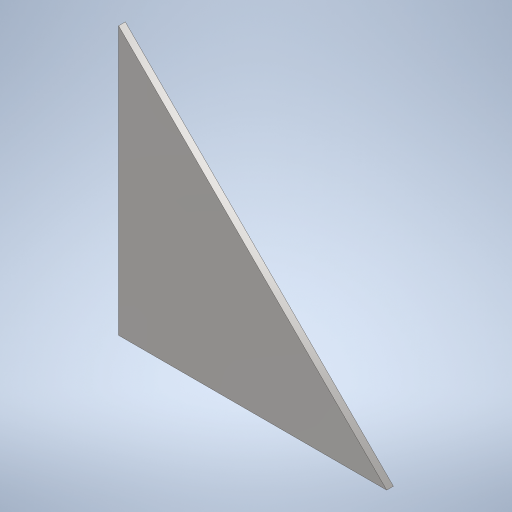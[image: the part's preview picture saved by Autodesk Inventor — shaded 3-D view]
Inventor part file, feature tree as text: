
AUTODESK INVENTOR PART (.ipt)
format: ipt  version: 2023 (Build 270158000, 158)  size: 222,208 bytes
history: native  units: mm
features: other x1, extrude x1, sketch x1
ambient origin geometry x8: Origin, YZ Plane, XZ Plane, XY Plane, X Axis, Y Axis, Z Axis, Center Point
bodies: Body1 (feature_tree)
feature tree (3):
  other  "Bryła1"
  extrude  "Wyciągnięcie proste1"  Depth=200.0mm
  sketch  "Szkic1"
